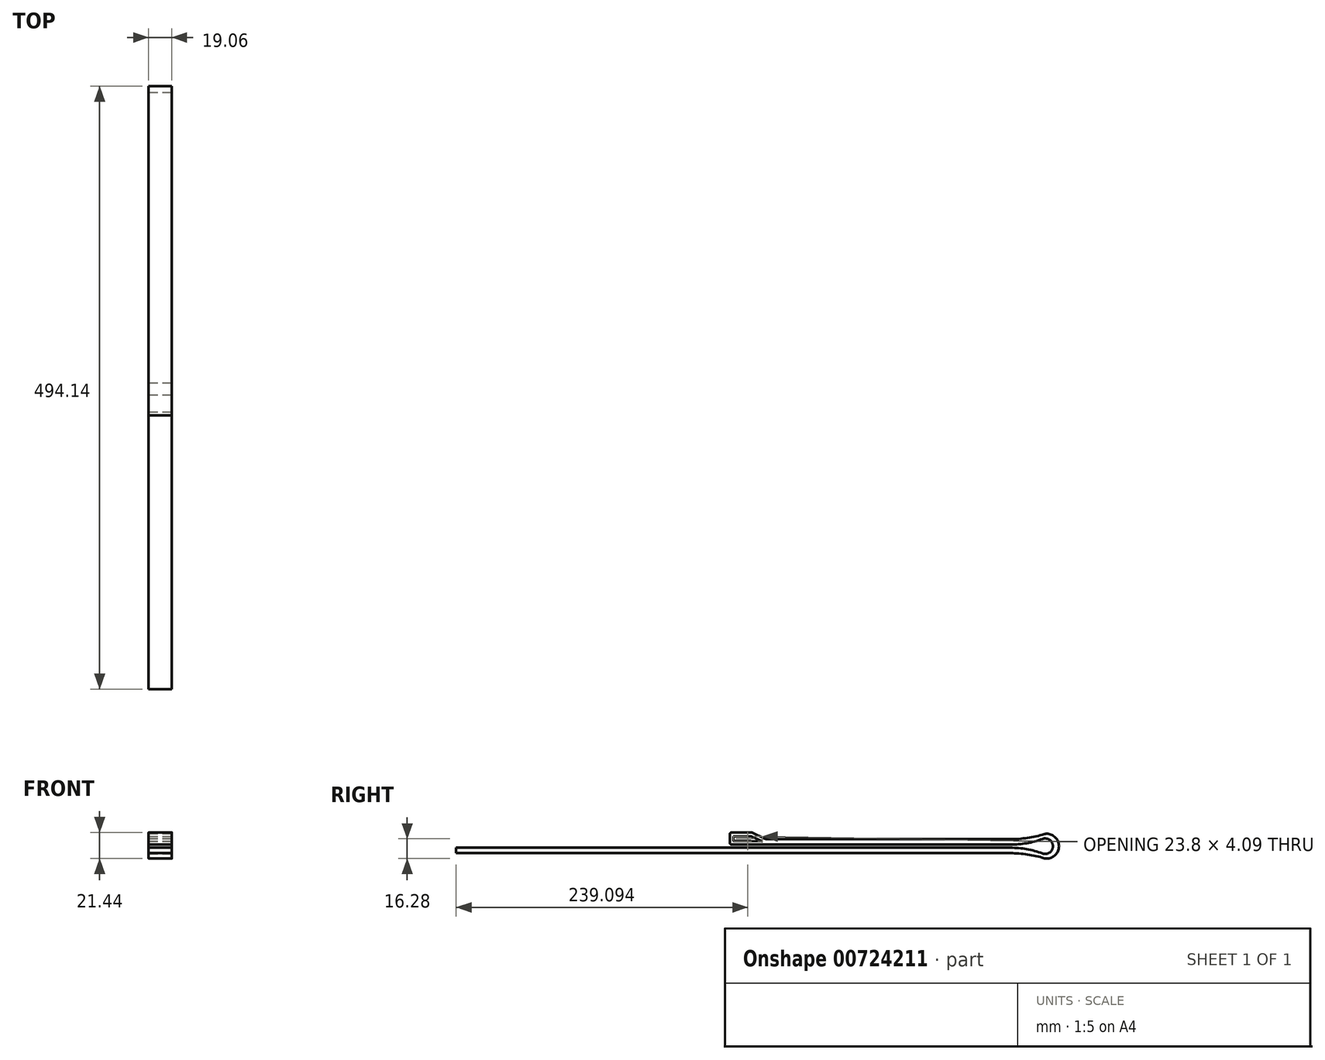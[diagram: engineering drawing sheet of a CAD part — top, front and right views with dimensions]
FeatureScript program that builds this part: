
annotation { "Feature Type Name" : "Feature", "Feature Type Description" : "" }
export const myFeature = defineFeature(function(context is Context, id is Id, definition is map)
    precondition{}
    {
        {
            var Q0;
            Q0=qCreatedBy(makeId("Right.planeOp"),FACE);
            var sketch = newSketch(context, id + "F0", { "sketchPlane" : qUnion([Q0])});
            skLineSegment(sketch, "E0.bottom", {"start": v(-254, 10.16) * mm, "end": v(254, 10.16) * mm});
            skLineSegment(sketch, "E0.top", {"start": v(-254, -10.16) * mm, "end": v(254, -10.16) * mm});
            skLineSegment(sketch, "E0.left", {"start": v(-254, 10.16) * mm, "end": v(-254, -10.16) * mm});
            skLineSegment(sketch, "E0.right", {"start": v(254, 10.16) * mm, "end": v(254, -10.16) * mm});
            skSolve(sketch);
        }
        {
            var Q0;
            Q0 = qSketchRegion(id + "F0", true);
            extrude(context, id + "F1", {"entities" : qUnion([Q0]), "oppositeDirection" : true, "depth" : 9.52 * mm, "offsetDistance" : 25.4 * mm, "hasSecondDirection" : true, "secondDirectionOppositeDirection" : false, "secondDirectionDepth" : 9.52 * mm});
        }
        {
            var Q0;
            Q0=makeQuery(id+"F1.opExtrude","CAP_FACE",FACE,{"disambiguationData":[OSD([sQuery(id+"F0.wireOp",EDGE,"E0.bottom"),sQuery(id+"F0.wireOp",EDGE,"E0.top"),sQuery(id+"F0.wireOp",EDGE,"E0.left"),sQuery(id+"F0.wireOp",EDGE,"E0.right")])],"isStart":true});
            var sketch = newSketch(context, id + "F2", { "sketchPlane" : qUnion([Q0])});
            skLineSegment(sketch, "E1", {"start": v(-279.2, 1.27) * mm, "end": v(228.8, 1.27) * mm});
            skLineSegment(sketch, "E2", {"start": v(228.8, 1.27) * mm, "end": v(228.8, -1.27) * mm});
            skLineSegment(sketch, "E3", {"start": v(228.8, -1.27) * mm, "end": v(-279.2, -1.27) * mm});
            skLineSegment(sketch, "E4", {"start": v(-279.2, 1.27) * mm, "end": v(-279.2, -1.27) * mm});
            skSolve(sketch);
        }
        {
            var Q0;
            Q0 = qSketchRegion(id + "F2", true);
            extrude(context, id + "F3", {"entities" : qUnion([Q0]), "operationType" : NewBodyOperationType.REMOVE, "oppositeDirection" : true, "depth" : 25.4 * mm, "offsetDistance" : 25.4 * mm});
        }
        {
            var Q0;
            Q0=makeQuery(id+"F1.opExtrude","CAP_FACE",FACE,{"disambiguationData":[OSD([sQuery(id+"F0.wireOp",EDGE,"E0.bottom"),sQuery(id+"F0.wireOp",EDGE,"E0.top"),sQuery(id+"F0.wireOp",EDGE,"E0.left"),sQuery(id+"F0.wireOp",EDGE,"E0.right")])],"isStart":true});
            var sketch = newSketch(context, id + "F4", { "sketchPlane" : qUnion([Q0])});
            skCircle(sketch, "E5", {"center": v(228.8, 0) * mm, "radius": 6.35 * mm});
            skSolve(sketch);
        }
        {
            var Q0;
            Q0 = qSketchRegion(id + "F4", true);
            extrude(context, id + "F5", {"entities" : qUnion([Q0]), "operationType" : NewBodyOperationType.REMOVE, "oppositeDirection" : true, "depth" : 25.4 * mm, "offsetDistance" : 25.4 * mm});
        }
        {
            var Q0;
            Q0=makeQuery(id+"F5.boolean.opBoolean","INTERSECT",EDGE,{"derivedFrom":[makeQuery(id+"F3.boolean.opBoolean","COPY",FACE,{"derivedFrom":makeQuery(id+"F3.opExtrude","SWEPT_FACE",FACE,{"disambiguationData":[OSD([sQuery(id+"F2.wireOp",EDGE,"E1")])]})}),makeQuery(id+"F5.opExtrude","SWEPT_FACE",FACE,{"disambiguationData":[OSD([sQuery(id+"F4.wireOp",EDGE,"E5")])]})]});
            var Q1;
            Q1=makeQuery(id+"F5.boolean.opBoolean","INTERSECT",EDGE,{"derivedFrom":[makeQuery(id+"F3.boolean.opBoolean","COPY",FACE,{"derivedFrom":makeQuery(id+"F3.opExtrude","SWEPT_FACE",FACE,{"disambiguationData":[OSD([sQuery(id+"F2.wireOp",EDGE,"E3")])]})}),makeQuery(id+"F5.opExtrude","SWEPT_FACE",FACE,{"disambiguationData":[OSD([sQuery(id+"F4.wireOp",EDGE,"E5")])]})]});
            fillet(context, id + "F6", {"entities" : qUnion([Q0, Q1]), "radius" : 76.2 * mm, "tangentPropagation" : true, "allowEdgeOverflow" : false});
        }
        {
            var Q0;
            Q0=makeQuery(id+"F1.opExtrude","CAP_FACE",FACE,{"disambiguationData":[OSD([sQuery(id+"F0.wireOp",EDGE,"E0.bottom"),sQuery(id+"F0.wireOp",EDGE,"E0.top"),sQuery(id+"F0.wireOp",EDGE,"E0.left"),sQuery(id+"F0.wireOp",EDGE,"E0.right")])],"isStart":true});
            var sketch = newSketch(context, id + "F7", { "sketchPlane" : qUnion([Q0])});
            skLineSegment(sketch, "E6", {"start": v(-254, 5.71) * mm, "end": v(200.3, 5.71) * mm});
            skLineSegment(sketch, "E7", {"start": v(200.3, -5.71) * mm, "end": v(-254, -5.72) * mm});
            skLineSegment(sketch, "E8", {"start": v(-254, -5.72) * mm, "end": v(-254, 5.71) * mm});
            skLineSegment(sketch, "E9", {"start": v(-254, -5.72) * mm, "end": v(-254, -13.4) * mm});
            skLineSegment(sketch, "E10", {"start": v(-254, -13.4) * mm, "end": v(265.42, -13.4) * mm});
            skLineSegment(sketch, "E11", {"start": v(265.42, -13.4) * mm, "end": v(265.42, 15.48) * mm});
            skLineSegment(sketch, "E12", {"start": v(265.42, 15.48) * mm, "end": v(-254, 15.48) * mm});
            skLineSegment(sketch, "E13", {"start": v(-254, 15.48) * mm, "end": v(-254, 5.71) * mm});
            skArc(sketch, "E14", {"start": v(200.3, 5.71) * mm, "mid": v(214.36, 6.76) * mm, "end": v(228.12, 9.88) * mm});
            skArc(sketch, "E15", {"start": v(228.12, -9.88) * mm, "mid": v(214.36, -6.76) * mm, "end": v(200.3, -5.71) * mm});
            skPoint(sketch, "E16.visualSharp", {"position": v(229.01, 10.16) * mm});
            skArc(sketch, "E16.filletArc", {"start": v(229.98, 10.16) * mm, "mid": v(229.04, 10.09) * mm, "end": v(228.12, 9.88) * mm});
            skPoint(sketch, "E17.visualSharp", {"position": v(229.01, -10.16) * mm});
            skArc(sketch, "E17.filletArc", {"start": v(228.12, -9.88) * mm, "mid": v(229.04, -10.09) * mm, "end": v(229.98, -10.16) * mm});
            skArc(sketch, "E18", {"start": v(229.98, -10.16) * mm, "mid": v(240.14, 0) * mm, "end": v(229.98, 10.16) * mm});
            skSolve(sketch);
        }
        {
            var Q0;
            {var subQ1=sQuery(id+"F4.wireOp",EDGE,"E5");Q0=makeQuery(id+"F7.imprint","IMPRINT",FACE,{"disambiguationData":[TD([[makeQuery(id+"F7.imprint","IMPRINT",EDGE,{"derivedFrom":makeQuery(id+"F5.boolean.opBoolean","COPY",EDGE,{"derivedFrom":makeQuery(id+"F5.opExtrude","CAP_EDGE",EDGE,{"disambiguationData":[OSD([subQ1])],"isStart":true})})}),1.0]])]});}
            var Q1;
            {var subQ0=sQuery(id+"F7.wireOp",EDGE,"E18");Q1=makeQuery(id+"F7.imprint","IMPRINT",FACE,{"disambiguationData":[TD([[makeQuery(id+"F7.imprint","IMPRINT",EDGE,{"derivedFrom":subQ0}),-1.0]])]});}
            var Q2;
            {var subQ4=sQuery(id+"F7.wireOp",EDGE,"E7");Q2=makeQuery(id+"F7.imprint","IMPRINT",FACE,{"disambiguationData":[TD([[makeQuery(id+"F7.imprint","IMPRINT",EDGE,{"derivedFrom":subQ4}),1.0]])]});}
            var Q3;
            {var subQ4=sQuery(id+"F7.wireOp",EDGE,"E6");Q3=makeQuery(id+"F7.imprint","IMPRINT",FACE,{"disambiguationData":[TD([[makeQuery(id+"F7.imprint","IMPRINT",EDGE,{"derivedFrom":subQ4}),1.0]])]});}
            extrude(context, id + "F8", {"entities" : qUnion([Q0, Q1, Q2, Q3]), "operationType" : NewBodyOperationType.REMOVE, "oppositeDirection" : true, "depth" : 25.4 * mm, "offsetDistance" : 25.4 * mm});
        }
        {
            var Q0;
            Q0=makeQuery(id+"F1.opExtrude","CAP_FACE",FACE,{"disambiguationData":[OSD([sQuery(id+"F0.wireOp",EDGE,"E0.bottom"),sQuery(id+"F0.wireOp",EDGE,"E0.top"),sQuery(id+"F0.wireOp",EDGE,"E0.left"),sQuery(id+"F0.wireOp",EDGE,"E0.right")])],"isStart":true});
            var sketch = newSketch(context, id + "F9", { "sketchPlane" : qUnion([Q0])});
            skLineSegment(sketch, "E19.bottom", {"start": v(-292.59, 44.02) * mm, "end": v(0, 44.02) * mm});
            skLineSegment(sketch, "E19.top", {"start": v(-292.59, 0) * mm, "end": v(0, 0) * mm});
            skLineSegment(sketch, "E19.left", {"start": v(-292.59, 44.02) * mm, "end": v(-292.59, 0) * mm});
            skLineSegment(sketch, "E19.right", {"start": v(0, 44.02) * mm, "end": v(0, 0) * mm});
            skSolve(sketch);
        }
        {
            var Q0;
            Q0 = qSketchRegion(id + "F9", true);
            extrude(context, id + "F10", {"entities" : qUnion([Q0]), "operationType" : NewBodyOperationType.REMOVE, "oppositeDirection" : true, "depth" : 25.4 * mm, "offsetDistance" : 25.4 * mm, "hasSecondDirection" : true, "secondDirectionOppositeDirection" : false, "secondDirectionDepth" : 25.4 * mm});
        }
        {
            var Q0;
            Q0=makeQuery(id+"F1.opExtrude","CAP_FACE",FACE,{"disambiguationData":[OSD([sQuery(id+"F0.wireOp",EDGE,"E0.bottom"),sQuery(id+"F0.wireOp",EDGE,"E0.top"),sQuery(id+"F0.wireOp",EDGE,"E0.left"),sQuery(id+"F0.wireOp",EDGE,"E0.right")])],"isStart":true});
            var sketch = newSketch(context, id + "F11", { "sketchPlane" : qUnion([Q0])});
            skLineSegment(sketch, "E20", {"start": v(0, 5.71) * mm, "end": v(-11.44, 11.15) * mm});
            skLineSegment(sketch, "E21", {"start": v(-11.99, 11.28) * mm, "end": v(-28.28, 11.28) * mm});
            skLineSegment(sketch, "E22", {"start": v(-29.55, 10) * mm, "end": v(-29.55, 2.54) * mm});
            skLineSegment(sketch, "E23", {"start": v(-28.28, 1.27) * mm, "end": v(0, 1.27) * mm});
            skPoint(sketch, "E24.visualSharp", {"position": v(-29.55, 11.28) * mm});
            skArc(sketch, "E24.filletArc", {"start": v(-28.28, 11.28) * mm, "mid": v(-29.18, 10.9) * mm, "end": v(-29.55, 10) * mm});
            skPoint(sketch, "E25.visualSharp", {"position": v(-29.55, 1.27) * mm});
            skArc(sketch, "E25.filletArc", {"start": v(-29.55, 2.54) * mm, "mid": v(-29.18, 1.64) * mm, "end": v(-28.28, 1.27) * mm});
            skPoint(sketch, "E26.visualSharp", {"position": v(-11.7, 11.28) * mm});
            skArc(sketch, "E26.filletArc", {"start": v(-11.44, 11.15) * mm, "mid": v(-11.7, 11.25) * mm, "end": v(-11.99, 11.28) * mm});
            skLineSegment(sketch, "E27.bottom", {"start": v(-26.55, 8.16) * mm, "end": v(-12.28, 8.16) * mm});
            skLineSegment(sketch, "E27.top", {"start": v(-26.55, 4.2) * mm, "end": v(-12.62, 4.2) * mm});
            skLineSegment(sketch, "E27.left", {"start": v(-26.8, 7.9) * mm, "end": v(-26.8, 4.45) * mm});
            skLineSegment(sketch, "E28", {"start": v(-12.62, 4.2) * mm, "end": v(-3, 4.08) * mm});
            skLineSegment(sketch, "E29", {"start": v(-3, 4.08) * mm, "end": v(-12.17, 8.14) * mm});
            skPoint(sketch, "E30.visualSharp", {"position": v(-26.8, 8.16) * mm});
            skArc(sketch, "E30.filletArc", {"start": v(-26.55, 8.16) * mm, "mid": v(-26.73, 8.09) * mm, "end": v(-26.8, 7.9) * mm});
            skPoint(sketch, "E31.visualSharp", {"position": v(-26.8, 4.2) * mm});
            skArc(sketch, "E31.filletArc", {"start": v(-26.8, 4.45) * mm, "mid": v(-26.73, 4.28) * mm, "end": v(-26.55, 4.2) * mm});
            skPoint(sketch, "E32.visualSharp", {"position": v(-12.22, 8.16) * mm});
            skArc(sketch, "E32.filletArc", {"start": v(-12.17, 8.14) * mm, "mid": v(-12.23, 8.16) * mm, "end": v(-12.28, 8.16) * mm});
            skLineSegment(sketch, "E33", {"start": v(0, 5.71) * mm, "end": v(2.02, 5.71) * mm});
            skLineSegment(sketch, "E34", {"start": v(2.02, 5.71) * mm, "end": v(2.02, 1.27) * mm});
            skLineSegment(sketch, "E35", {"start": v(2.02, 1.27) * mm, "end": v(0, 1.27) * mm});
            skSolve(sketch);
        }
        {
            var Q0;
            Q0=makeQuery(id+"F11.imprint","IMPRINT",FACE,{"disambiguationData":[TD([[makeQuery(id+"F11.imprint","IMPRINT",EDGE,{"derivedFrom":sQuery(id+"F11.wireOp",EDGE,"E20")}),1.0]])]});
            extrude(context, id + "F12", {"entities" : qUnion([Q0]), "operationType" : NewBodyOperationType.ADD, "oppositeDirection" : true, "depth" : 19.05 * mm, "offsetDistance" : 25.4 * mm});
        }
        {
            var Q0;
            {var subQ0=sQuery(id+"F9.wireOp",EDGE,"E19.right");Q0=makeQuery(id+"F12.boolean.opBoolean","MERGE",EDGE,{"derivedFrom":[makeQuery(id+"F10.boolean.opBoolean","INTERSECT",EDGE,{"derivedFrom":[makeQuery(id+"F8.boolean.opBoolean","COPY",FACE,{"derivedFrom":makeQuery(id+"F8.opExtrude","SWEPT_FACE",FACE,{"disambiguationData":[OSD([sQuery(id+"F7.wireOp",EDGE,"E6")])]})}),makeQuery(id+"F10.opExtrude","SWEPT_FACE",FACE,{"disambiguationData":[OSD([subQ0])]})]}),makeQuery(id+"F12.opExtrude","SWEPT_EDGE",EDGE,{"disambiguationData":[OSD([sQuery(id+"F0.wireOp",EDGE,"E0.bottom"),sQuery(id+"F0.wireOp",EDGE,"E0.top"),sQuery(id+"F0.wireOp",EDGE,"E0.left"),sQuery(id+"F0.wireOp",EDGE,"E0.right"),subQ0,sQuery(id+"F11.wireOp",EDGE,"E20"),sQuery(id+"F11.wireOp",EDGE,"E33")])]})]});}
            fillet(context, id + "F13", {"entities" : qUnion([Q0]), "radius" : 5.08 * mm, "tangentPropagation" : true, "allowEdgeOverflow" : false});
        }
    });
